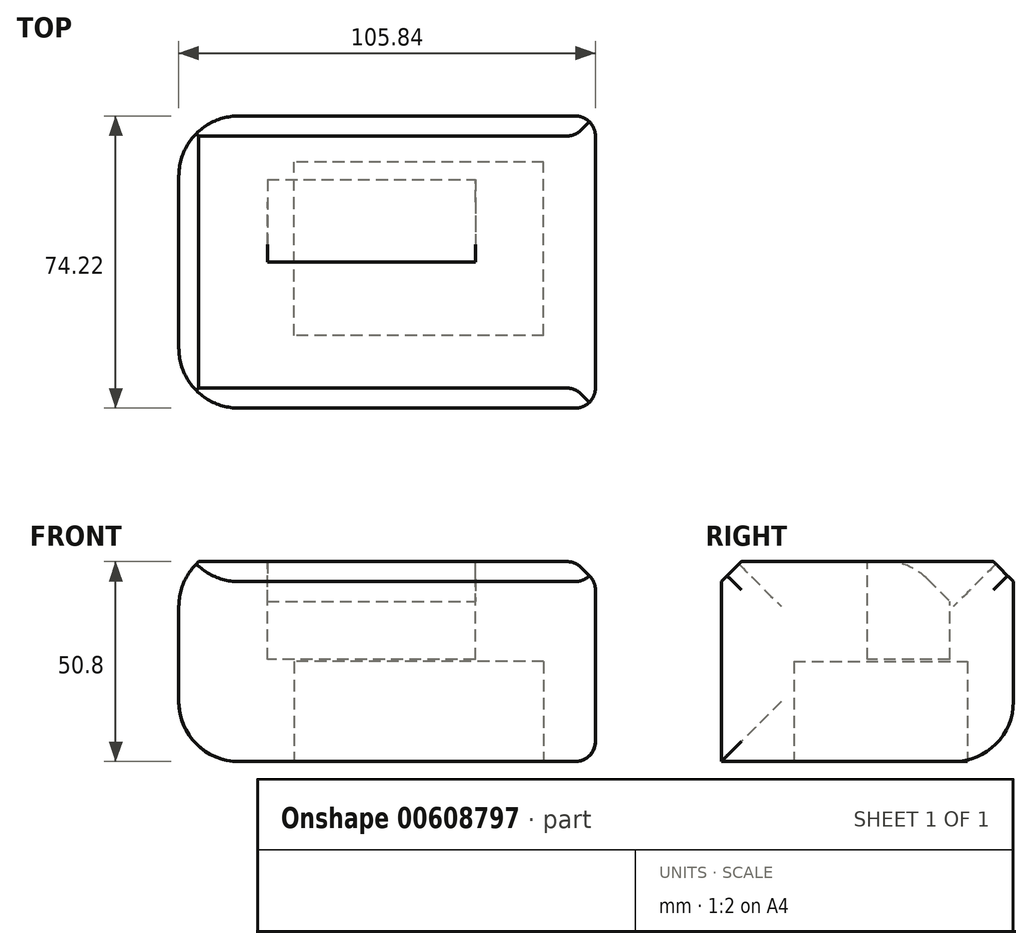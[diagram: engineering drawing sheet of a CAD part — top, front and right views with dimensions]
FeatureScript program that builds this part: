
annotation { "Feature Type Name" : "Feature", "Feature Type Description" : "" }
export const myFeature = defineFeature(function(context is Context, id is Id, definition is map)
    precondition{}
    {
        {
            var Q0;
            Q0=qCreatedBy(makeId("Top.planeOp"),FACE);
            var sketch = newSketch(context, id + "F0", { "sketchPlane" : qUnion([Q0])});
            skLineSegment(sketch, "E0.bottom", {"start": v(-40.33, 36.3) * mm, "end": v(65.51, 36.3) * mm});
            skLineSegment(sketch, "E0.top", {"start": v(-40.33, -37.93) * mm, "end": v(65.51, -37.93) * mm});
            skLineSegment(sketch, "E0.left", {"start": v(-40.33, 36.3) * mm, "end": v(-40.33, -37.93) * mm});
            skLineSegment(sketch, "E0.right", {"start": v(65.51, 36.3) * mm, "end": v(65.51, -37.93) * mm});
            skSolve(sketch);
        }
        {
            var Q0;
            Q0=makeQuery(id+"F0.imprint","IMPRINT",FACE,{"disambiguationData":[TD([[makeQuery(id+"F0.imprint","IMPRINT",EDGE,{"derivedFrom":sQuery(id+"F0.wireOp",EDGE,"E0.bottom")}),-1.0]])]});
            extrude(context, id + "F1", {"entities" : qUnion([Q0]), "depth" : 25.4 * mm, "offsetDistance" : 25.4 * mm, "hasSecondDirection" : true, "secondDirectionOppositeDirection" : true, "secondDirectionDepth" : 25.4 * mm});
        }
        {
            var Q0;
            Q0=makeQuery(id+"F1.opExtrude","CAP_FACE",FACE,{"disambiguationData":[OSD([sQuery(id+"F0.wireOp",EDGE,"E0.bottom"),sQuery(id+"F0.wireOp",EDGE,"E0.top"),sQuery(id+"F0.wireOp",EDGE,"E0.left"),sQuery(id+"F0.wireOp",EDGE,"E0.right")])],"isStart":false});
            var sketch = newSketch(context, id + "F2", { "sketchPlane" : qUnion([Q0])});
            skPoint(sketch, "E1.oppositeSnap0", {"position": v(65.51, -0.82) * mm});
            skLineSegment(sketch, "E1.bottom", {"start": v(35.06, 20.15) * mm, "end": v(-17.8, 20.15) * mm});
            skLineSegment(sketch, "E1.top", {"start": v(35.06, -0.82) * mm, "end": v(-17.8, -0.82) * mm});
            skLineSegment(sketch, "E1.left", {"start": v(35.06, 20.15) * mm, "end": v(35.06, -0.82) * mm});
            skLineSegment(sketch, "E1.right", {"start": v(-17.8, 20.15) * mm, "end": v(-17.8, -0.82) * mm});
            skSolve(sketch);
        }
        {
            var Q0;
            Q0 = qSketchRegion(id + "F2", true);
            var Q1;
            Q1=makeQuery(id+"F2.imprint","IMPRINT",FACE,{"disambiguationData":[TD([[makeQuery(id+"F2.imprint","IMPRINT",EDGE,{"derivedFrom":sQuery(id+"F2.wireOp",EDGE,"E1.bottom")}),1.0]])]});
            extrude(context, id + "F3", {"entities" : qUnion([Q0, Q1]), "oppositeDirection" : true, "depth" : 24.9 * mm, "offsetDistance" : 25.4 * mm});
        }
        {
            var Q0;
            Q0=makeQuery(id+"F1.opExtrude","CAP_FACE",FACE,{"disambiguationData":[OSD([sQuery(id+"F0.wireOp",EDGE,"E0.bottom"),sQuery(id+"F0.wireOp",EDGE,"E0.top"),sQuery(id+"F0.wireOp",EDGE,"E0.left"),sQuery(id+"F0.wireOp",EDGE,"E0.right")])],"isStart":true});
            var sketch = newSketch(context, id + "F4", { "sketchPlane" : qUnion([Q0])});
            skLineSegment(sketch, "E2.bottom", {"start": v(52.36, 19.52) * mm, "end": v(-11.05, 19.52) * mm});
            skLineSegment(sketch, "E2.top", {"start": v(52.36, -24.56) * mm, "end": v(-11.05, -24.56) * mm});
            skLineSegment(sketch, "E2.left", {"start": v(52.36, 19.52) * mm, "end": v(52.36, -24.56) * mm});
            skLineSegment(sketch, "E2.right", {"start": v(-11.05, 19.52) * mm, "end": v(-11.05, -24.56) * mm});
            skSolve(sketch);
        }
        {
            var Q0;
            Q0=makeQuery(id+"F4.imprint","IMPRINT",FACE,{"disambiguationData":[TD([[makeQuery(id+"F4.imprint","IMPRINT",EDGE,{"derivedFrom":sQuery(id+"F4.wireOp",EDGE,"E2.bottom")}),1.0]])]});
            extrude(context, id + "F5", {"entities" : qUnion([Q0]), "oppositeDirection" : true, "depth" : 25.4 * mm, "offsetDistance" : 25.4 * mm});
        }
        {
            var Q0;
            Q0=makeQuery(id+"F3.opExtrude","CAP_EDGE",EDGE,{"disambiguationData":[OSD([sQuery(id+"F2.wireOp",EDGE,"E1.bottom")])],"isStart":true});
            chamfer(context, id + "F6", {"entities" : qUnion([Q0]), "chamferType" : ChamferType.OFFSET_ANGLE, "width" : 10.16 * mm, "oppositeDirection" : true, "angle" : 45 * degree, "tangentPropagation" : true});
        }
        {
            var Q0;
            Q0=makeQuery(id+"F1.opExtrude","CAP_FACE",FACE,{"disambiguationData":[OSD([sQuery(id+"F0.wireOp",EDGE,"E0.bottom"),sQuery(id+"F0.wireOp",EDGE,"E0.top"),sQuery(id+"F0.wireOp",EDGE,"E0.left"),sQuery(id+"F0.wireOp",EDGE,"E0.right")])],"isStart":false});
            chamfer(context, id + "F7", {"entities" : qUnion([Q0]), "chamferType" : ChamferType.TWO_OFFSETS, "width1" : 5.08 * mm, "oppositeDirection" : true, "width2" : 5.08 * mm, "tangentPropagation" : true});
        }
        {
            var Q0;
            {var subQ0=sQuery(id+"F0.wireOp",EDGE,"E0.right");Q0=makeQuery(id+"F7.opChamfer","BLEND_EDGE",EDGE,{"blendedFrom":[makeQuery(id+"F1.opExtrude","CAP_EDGE",EDGE,{"disambiguationData":[OSD([subQ0])],"isStart":false}),makeQuery(id+"F1.opExtrude","CAP_FACE",FACE,{"disambiguationData":[OSD([sQuery(id+"F0.wireOp",EDGE,"E0.bottom"),sQuery(id+"F0.wireOp",EDGE,"E0.top"),sQuery(id+"F0.wireOp",EDGE,"E0.left"),subQ0])],"isStart":false})],"blendedInto":[makeQuery(id+"F1.opExtrude","CAP_FACE",FACE,{"disambiguationData":[OSD([sQuery(id+"F0.wireOp",EDGE,"E0.bottom"),sQuery(id+"F0.wireOp",EDGE,"E0.top"),sQuery(id+"F0.wireOp",EDGE,"E0.left"),subQ0])],"isStart":false})]});}
            fillet(context, id + "F8", {"entities" : qUnion([Q0]), "radius" : 5.08 * mm, "tangentPropagation" : true, "allowEdgeOverflow" : false});
        }
        {
            var Q0;
            Q0=makeQuery(id+"F1.opExtrude","SWEPT_FACE",FACE,{"disambiguationData":[OSD([sQuery(id+"F0.wireOp",EDGE,"E0.right")])]});
            var Q1;
            {var subQ0=sQuery(id+"F0.wireOp",EDGE,"E0.right");Q1=makeQuery(id+"F8.opFillet","BLEND_EDGE",EDGE,{"blendedFrom":[makeQuery(id+"F7.opChamfer","BLEND_EDGE",EDGE,{"blendedFrom":[makeQuery(id+"F1.opExtrude","CAP_EDGE",EDGE,{"disambiguationData":[OSD([subQ0])],"isStart":false}),makeQuery(id+"F1.opExtrude","CAP_FACE",FACE,{"disambiguationData":[OSD([sQuery(id+"F0.wireOp",EDGE,"E0.bottom"),sQuery(id+"F0.wireOp",EDGE,"E0.top"),sQuery(id+"F0.wireOp",EDGE,"E0.left"),subQ0])],"isStart":false})],"blendedInto":[makeQuery(id+"F1.opExtrude","CAP_FACE",FACE,{"disambiguationData":[OSD([sQuery(id+"F0.wireOp",EDGE,"E0.bottom"),sQuery(id+"F0.wireOp",EDGE,"E0.top"),sQuery(id+"F0.wireOp",EDGE,"E0.left"),subQ0])],"isStart":false})]}),makeQuery(id+"F7.opChamfer","BLEND_FACE",FACE,{"disambiguationData":[OSD([subQ0])]})],"blendedInto":[makeQuery(id+"F7.opChamfer","BLEND_FACE",FACE,{"disambiguationData":[OSD([subQ0])]})]});}
            fillet(context, id + "F9", {"entities" : qUnion([Q0, Q1]), "radius" : 5.08 * mm, "tangentPropagation" : true, "allowEdgeOverflow" : false});
        }
        {
            var Q0;
            Q0=makeQuery(id+"F1.opExtrude","SWEPT_FACE",FACE,{"disambiguationData":[OSD([sQuery(id+"F0.wireOp",EDGE,"E0.left")])]});
            fillet(context, id + "F10", {"entities" : qUnion([Q0]), "radius" : 15.24 * mm, "tangentPropagation" : true, "allowEdgeOverflow" : false});
        }
        {
            var Q0;
            {var subQ0=sQuery(id+"F0.wireOp",EDGE,"E0.right");Q0=makeQuery(id+"F9.opFillet","BLEND_EDGE",EDGE,{"blendedFrom":[makeQuery(id+"F1.opExtrude","SWEPT_EDGE",EDGE,{"disambiguationData":[OSD([sQuery(id+"F0.wireOp",EDGE,"E0.bottom"),subQ0])]}),makeQuery(id+"F1.opExtrude","SWEPT_FACE",FACE,{"disambiguationData":[OSD([subQ0])]})],"blendedInto":[makeQuery(id+"F1.opExtrude","SWEPT_FACE",FACE,{"disambiguationData":[OSD([subQ0])]})]});}
            var Q1;
            Q1=makeQuery(id+"F1.opExtrude","CAP_EDGE",EDGE,{"disambiguationData":[OSD([sQuery(id+"F0.wireOp",EDGE,"E0.bottom")])],"isStart":true});
            var Q2;
            {var subQ0=sQuery(id+"F0.wireOp",EDGE,"E0.bottom");Q2=makeQuery(id+"F9.opFillet","BLEND_EDGE",EDGE,{"blendedFrom":[makeQuery(id+"F1.opExtrude","SWEPT_EDGE",EDGE,{"disambiguationData":[OSD([subQ0,sQuery(id+"F0.wireOp",EDGE,"E0.right")])]}),makeQuery(id+"F1.opExtrude","SWEPT_FACE",FACE,{"disambiguationData":[OSD([subQ0])]})],"blendedInto":[makeQuery(id+"F1.opExtrude","SWEPT_FACE",FACE,{"disambiguationData":[OSD([subQ0])]})]});}
            fillet(context, id + "F11", {"entities" : qUnion([Q0, Q1, Q2]), "radius" : 15.24 * mm, "tangentPropagation" : true, "allowEdgeOverflow" : false});
        }
        {
            var Q0;
            {var subQ0=sQuery(id+"F2.wireOp",EDGE,"E1.bottom");Q0=makeQuery(id+"F6.opChamfer","BLEND_EDGE",EDGE,{"blendedFrom":[makeQuery(id+"F3.opExtrude","CAP_EDGE",EDGE,{"disambiguationData":[OSD([subQ0])],"isStart":true}),makeQuery(id+"F3.opExtrude","CAP_FACE",FACE,{"disambiguationData":[OSD([subQ0,sQuery(id+"F2.wireOp",EDGE,"E1.top"),sQuery(id+"F2.wireOp",EDGE,"E1.left"),sQuery(id+"F2.wireOp",EDGE,"E1.right")])],"isStart":true})],"blendedInto":[makeQuery(id+"F3.opExtrude","CAP_FACE",FACE,{"disambiguationData":[OSD([subQ0,sQuery(id+"F2.wireOp",EDGE,"E1.top"),sQuery(id+"F2.wireOp",EDGE,"E1.left"),sQuery(id+"F2.wireOp",EDGE,"E1.right")])],"isStart":true})]});}
            fillet(context, id + "F12", {"entities" : qUnion([Q0]), "radius" : 15.24 * mm, "tangentPropagation" : true, "rho" : 0.5, "crossSection" : FilletCrossSection.CONIC, "allowEdgeOverflow" : false});
        }
    });
